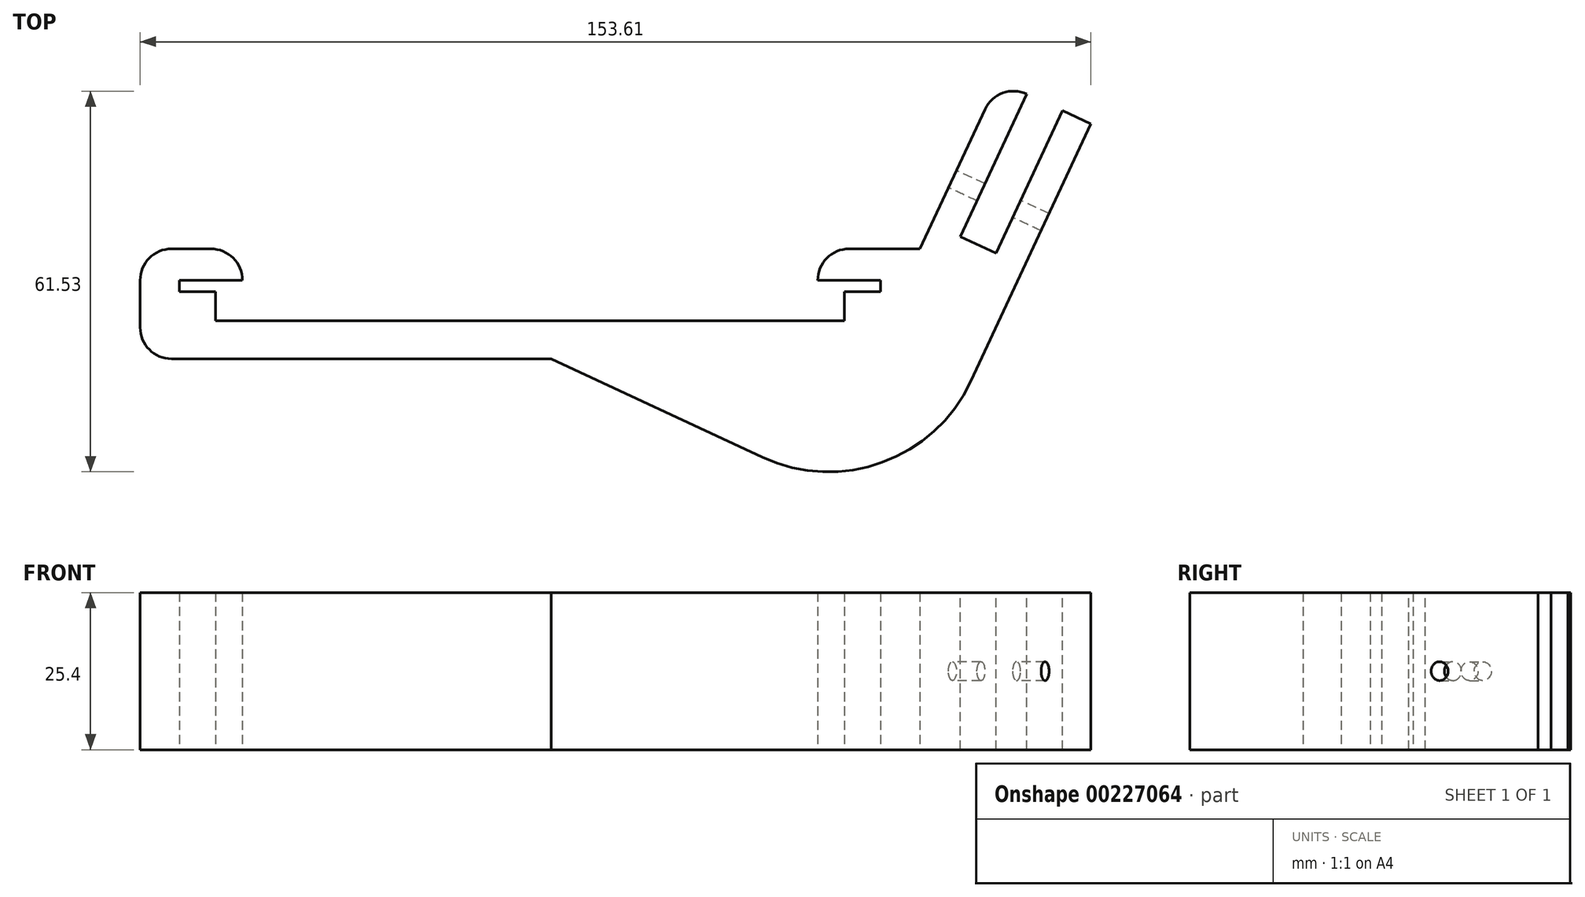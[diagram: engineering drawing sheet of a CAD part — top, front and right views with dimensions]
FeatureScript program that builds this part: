
annotation { "Feature Type Name" : "Feature", "Feature Type Description" : "" }
export const myFeature = defineFeature(function(context is Context, id is Id, definition is map)
    precondition{}
    {
        {
            var Q0;
            Q0=qCreatedBy(makeId("Top.planeOp"),FACE);
            var sketch = newSketch(context, id + "F0", { "sketchPlane" : qUnion([Q0])});
            skLineSegment(sketch, "E0.bottom", {"start": v(-63, 8.9) * mm, "end": v(63, 8.9) * mm});
            skLineSegment(sketch, "E0.top", {"start": v(-63, -8.9) * mm, "end": v(63, -8.9) * mm});
            skLineSegment(sketch, "E0.left", {"start": v(-63, 8.9) * mm, "end": v(-63, -8.9) * mm});
            skLineSegment(sketch, "E0.right", {"start": v(63, 8.9) * mm, "end": v(63, -8.9) * mm});
            skPoint(sketch, "E0.middle", {"position": v(0, 0) * mm});
            skLineSegment(sketch, "E1", {"start": v(-56.64, 8.9) * mm, "end": v(-56.64, -8.9) * mm, "construction": true});
            skLineSegment(sketch, "E2", {"start": v(56.64, 8.9) * mm, "end": v(56.64, -8.9) * mm, "construction": true});
            skLineSegment(sketch, "E3", {"start": v(-63, 3.81) * mm, "end": v(63, 3.81) * mm, "construction": true});
            skLineSegment(sketch, "E4", {"start": v(-63, 1.98) * mm, "end": v(63, 1.98) * mm, "construction": true});
            skLineSegment(sketch, "E5", {"start": v(-46.48, 8.9) * mm, "end": v(-46.48, -8.9) * mm, "construction": true});
            skLineSegment(sketch, "E6", {"start": v(46.48, 8.9) * mm, "end": v(46.48, -8.9) * mm, "construction": true});
            skLineSegment(sketch, "E7", {"start": v(-63, -2.72) * mm, "end": v(63, -2.72) * mm, "construction": true});
            skLineSegment(sketch, "E8", {"start": v(-50.8, 8.9) * mm, "end": v(-50.8, -8.9) * mm, "construction": true});
            skLineSegment(sketch, "E9", {"start": v(50.8, 8.9) * mm, "end": v(50.8, -8.9) * mm, "construction": true});
            skLineSegment(sketch, "E10", {"start": v(-46.48, 8.9) * mm, "end": v(-46.48, 3.81) * mm});
            skLineSegment(sketch, "E11", {"start": v(-46.48, 3.81) * mm, "end": v(-56.64, 3.81) * mm});
            skLineSegment(sketch, "E12", {"start": v(-56.64, 3.81) * mm, "end": v(-56.64, 1.98) * mm});
            skLineSegment(sketch, "E13", {"start": v(-56.64, 1.98) * mm, "end": v(-50.8, 1.98) * mm});
            skLineSegment(sketch, "E14", {"start": v(-50.8, 1.98) * mm, "end": v(-50.8, -2.72) * mm});
            skLineSegment(sketch, "E15", {"start": v(-50.8, -2.72) * mm, "end": v(50.8, -2.72) * mm});
            skLineSegment(sketch, "E16", {"start": v(50.8, -2.72) * mm, "end": v(50.8, 1.98) * mm});
            skPoint(sketch, "E16.endSnap0", {"position": v(50.8, 0) * mm});
            skLineSegment(sketch, "E17", {"start": v(50.8, 1.98) * mm, "end": v(56.64, 1.98) * mm});
            skLineSegment(sketch, "E18", {"start": v(56.64, 1.98) * mm, "end": v(56.64, 3.81) * mm});
            skLineSegment(sketch, "E19", {"start": v(56.64, 3.81) * mm, "end": v(46.48, 3.81) * mm});
            skLineSegment(sketch, "E20", {"start": v(46.48, 3.81) * mm, "end": v(46.48, 8.9) * mm});
            skSolve(sketch);
        }
        {
            var Q0;
            Q0=makeQuery(id+"F0.imprint","IMPRINT",FACE,{"disambiguationData":[TD([[makeQuery(id+"F0.imprint","IMPRINT",EDGE,{"derivedFrom":sQuery(id+"F0.wireOp",EDGE,"E0.top")}),1.0]])]});
            extrude(context, id + "F1", {"entities" : qUnion([Q0]), "depth" : 25.4 * mm});
        }
        {
            var Q0;
            Q0=makeQuery(id+"F1.opExtrude","CAP_FACE",FACE,{"disambiguationData":[OSD([sQuery(id+"F0.wireOp",EDGE,"E0.bottom"),sQuery(id+"F0.wireOp",EDGE,"E0.top"),sQuery(id+"F0.wireOp",EDGE,"E0.left"),sQuery(id+"F0.wireOp",EDGE,"E0.right"),sQuery(id+"F0.wireOp",EDGE,"E10"),sQuery(id+"F0.wireOp",EDGE,"E11"),sQuery(id+"F0.wireOp",EDGE,"E12"),sQuery(id+"F0.wireOp",EDGE,"E13"),sQuery(id+"F0.wireOp",EDGE,"E14"),sQuery(id+"F0.wireOp",EDGE,"E15"),sQuery(id+"F0.wireOp",EDGE,"E16"),sQuery(id+"F0.wireOp",EDGE,"E17"),sQuery(id+"F0.wireOp",EDGE,"E18"),sQuery(id+"F0.wireOp",EDGE,"E19"),sQuery(id+"F0.wireOp",EDGE,"E20")])],"isStart":false});
            var sketch = newSketch(context, id + "F2", { "sketchPlane" : qUnion([Q0])});
            skLineSegment(sketch, "E21", {"start": v(63, 8.89) * mm, "end": v(75.66, 36.05) * mm});
            skLineSegment(sketch, "E22", {"start": v(75.66, 36.05) * mm, "end": v(90.62, 29.07) * mm});
            skLineSegment(sketch, "E23", {"start": v(90.62, 29.07) * mm, "end": v(60.5, -35.5) * mm});
            skLineSegment(sketch, "E24", {"start": v(60.5, -35.5) * mm, "end": v(3.44, -8.9) * mm});
            skLineSegment(sketch, "E25", {"start": v(80.26, 33.9) * mm, "end": v(69.53, 10.88) * mm});
            skLineSegment(sketch, "E26", {"start": v(69.53, 10.88) * mm, "end": v(75.28, 8.2) * mm});
            skLineSegment(sketch, "E27", {"start": v(75.28, 8.2) * mm, "end": v(86.02, 31.22) * mm});
            skSolve(sketch);
        }
        {
            var Q0;
            {var subQ6=sQuery(id+"F2.wireOp",EDGE,"E21");Q0=makeQuery(id+"F2.imprint","IMPRINT",FACE,{"disambiguationData":[TD([[makeQuery(id+"F2.imprint","IMPRINT",EDGE,{"derivedFrom":subQ6}),-1.0]])]});}
            extrude(context, id + "F3", {"entities" : qUnion([Q0]), "operationType" : NewBodyOperationType.ADD, "oppositeDirection" : true, "depth" : 25.4 * mm});
        }
        {
            var Q0;
            Q0=makeQuery(id+"F3.opExtrude","SWEPT_EDGE",EDGE,{"disambiguationData":[OSD([sQuery(id+"F2.wireOp",EDGE,"E23"),sQuery(id+"F2.wireOp",EDGE,"E24")])]});
            fillet(context, id + "F4", {"entities" : qUnion([Q0]), "radius" : 25.4 * mm, "tangentPropagation" : true, "allowEdgeOverflow" : false});
        }
        {
            var Q0;
            Q0=makeQuery(id+"F1.opExtrude","SWEPT_EDGE",EDGE,{"disambiguationData":[OSD([sQuery(id+"F0.wireOp",EDGE,"E0.top"),sQuery(id+"F0.wireOp",EDGE,"E0.left")])]});
            var Q1;
            Q1=makeQuery(id+"F1.opExtrude","SWEPT_EDGE",EDGE,{"disambiguationData":[OSD([sQuery(id+"F0.wireOp",EDGE,"E0.bottom"),sQuery(id+"F0.wireOp",EDGE,"E0.left")])]});
            var Q2;
            Q2=makeQuery(id+"F3.opExtrude","SWEPT_EDGE",EDGE,{"disambiguationData":[OSD([sQuery(id+"F2.wireOp",EDGE,"E21"),sQuery(id+"F2.wireOp",EDGE,"E22")])]});
            var Q3;
            Q3=makeQuery(id+"F1.opExtrude","SWEPT_EDGE",EDGE,{"disambiguationData":[OSD([sQuery(id+"F0.wireOp",EDGE,"E0.bottom"),sQuery(id+"F0.wireOp",EDGE,"E20")])]});
            var Q4;
            Q4=makeQuery(id+"F1.opExtrude","SWEPT_EDGE",EDGE,{"disambiguationData":[OSD([sQuery(id+"F0.wireOp",EDGE,"E0.bottom"),sQuery(id+"F0.wireOp",EDGE,"E10")])]});
            fillet(context, id + "F5", {"entities" : qUnion([Q0, Q1, Q2, Q3, Q4]), "radius" : 5.08 * mm, "tangentPropagation" : true, "allowEdgeOverflow" : false});
        }
        {
            var Q0;
            Q0=makeQuery(id+"F3.opExtrude","SWEPT_FACE",FACE,{"disambiguationData":[OSD([sQuery(id+"F2.wireOp",EDGE,"E21")])]});
            var sketch = newSketch(context, id + "F6", { "sketchPlane" : qUnion([Q0])});
            skLineSegment(sketch, "E28", {"start": v(-47.12, 0) * mm, "end": v(-47.12, 25.4) * mm, "construction": true});
            skCircle(sketch, "E29", {"center": v(-47.12, 12.7) * mm, "radius": 1.52 * mm});
            skSolve(sketch);
        }
        {
            var Q0;
            Q0=makeQuery(id+"F6.imprint","IMPRINT",FACE,{"disambiguationData":[TD([[makeQuery(id+"F6.imprint","IMPRINT",EDGE,{"derivedFrom":sQuery(id+"F6.wireOp",EDGE,"E29")}),1.0]])]});
            extrude(context, id + "F7", {"entities" : qUnion([Q0]), "operationType" : NewBodyOperationType.REMOVE, "oppositeDirection" : true, "depth" : 25.4 * mm});
        }
    });
